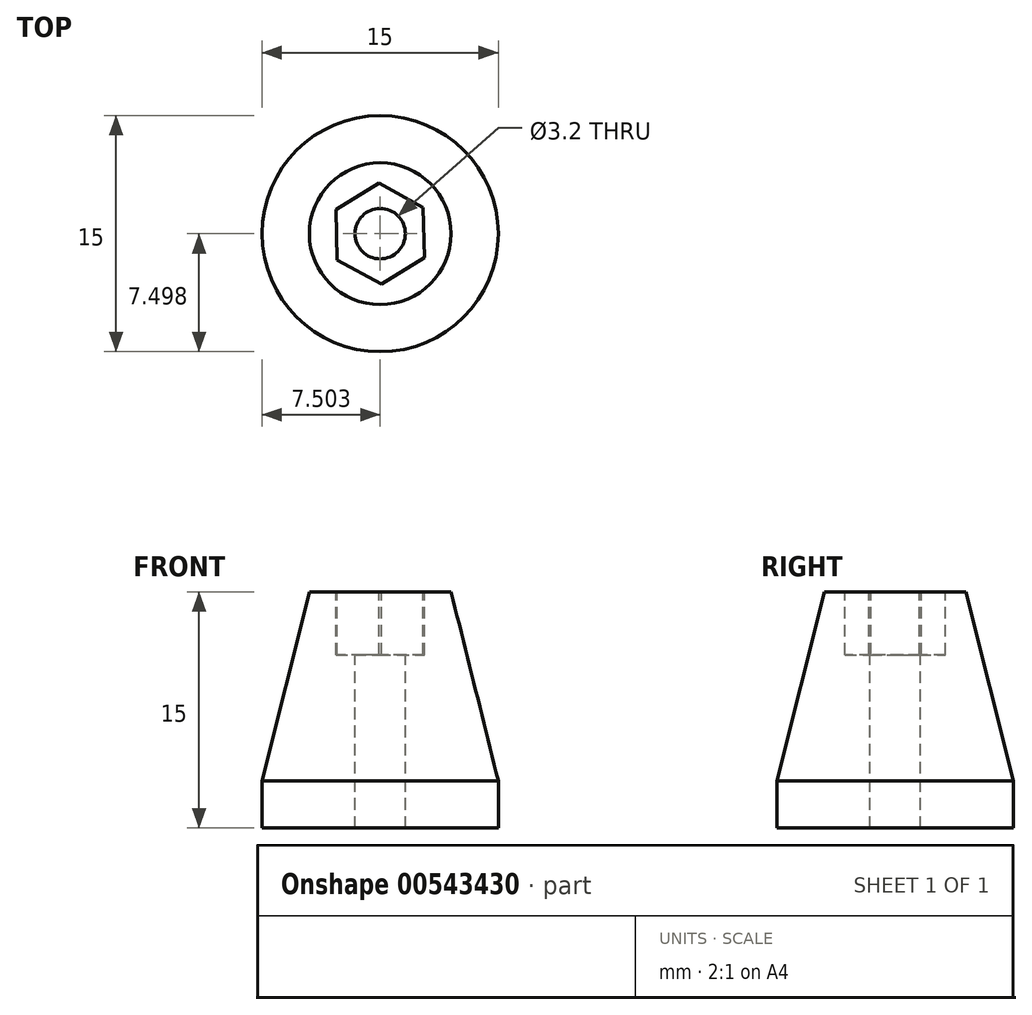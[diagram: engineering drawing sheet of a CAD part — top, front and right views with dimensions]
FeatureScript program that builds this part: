
annotation { "Feature Type Name" : "Feature", "Feature Type Description" : "" }
export const myFeature = defineFeature(function(context is Context, id is Id, definition is map)
    precondition{}
    {
        {
            var Q0;
            Q0=qCreatedBy(makeId("Top.planeOp"),FACE);
            var sketch = newSketch(context, id + "F0", { "sketchPlane" : qUnion([Q0])});
            skCircle(sketch, "E0", {"center": v(-11.83, 14.6) * mm, "radius": 7.5 * mm});
            skSolve(sketch);
        }
        {
            var Q0;
            Q0=makeQuery(id+"F0.imprint","IMPRINT",FACE,{"disambiguationData":[TD([[makeQuery(id+"F0.imprint","IMPRINT",EDGE,{"derivedFrom":sQuery(id+"F0.wireOp",EDGE,"E0")}),1.0]])]});
            extrude(context, id + "F1", {"entities" : qUnion([Q0]), "depth" : 3 * mm, "offsetDistance" : 25 * mm});
        }
        {
            var Q0;
            Q0=makeQuery(id+"F1.opExtrude","CAP_FACE",FACE,{"disambiguationData":[OSD([sQuery(id+"F0.wireOp",EDGE,"E0")])],"isStart":false});
            var sketch = newSketch(context, id + "F2", { "sketchPlane" : qUnion([Q0])});
            skCircle(sketch, "E1", {"center": v(-11.83, 14.6) * mm, "radius": 7.5 * mm});
            skSolve(sketch);
        }
        {
            var Q0;
            Q0 = qSketchRegion(id + "F2", true);
            var Q1;
            Q1=makeQuery(id+"F2.imprint","IMPRINT",FACE,{"disambiguationData":[TD([[makeQuery(id+"F2.imprint","IMPRINT",EDGE,{"derivedFrom":sQuery(id+"F2.wireOp",EDGE,"E1")}),1.0]])]});
            extrude(context, id + "F3", {"entities" : qUnion([Q0, Q1]), "operationType" : NewBodyOperationType.ADD, "depth" : 12 * mm, "offsetDistance" : 25 * mm});
        }
        {
            var Q0;
            Q0=makeQuery(id+"F3.opExtrude","CAP_FACE",FACE,{"disambiguationData":[OSD([sQuery(id+"F2.wireOp",EDGE,"E1")])],"isStart":false});
            chamfer(context, id + "F4", {"entities" : qUnion([Q0]), "chamferType" : ChamferType.TWO_OFFSETS, "width1" : 3 * mm, "oppositeDirection" : false, "width2" : 12 * mm});
        }
        {
            var Q0;
            Q0=makeQuery(id+"F3.opExtrude","CAP_FACE",FACE,{"disambiguationData":[OSD([sQuery(id+"F2.wireOp",EDGE,"E1")])],"isStart":false});
            var sketch = newSketch(context, id + "F5", { "sketchPlane" : qUnion([Q0])});
            skCircle(sketch, "E2.cCircle", {"center": v(-11.83, 14.6) * mm, "radius": 2.77 * mm, "construction": true});
            skLineSegment(sketch, "E2.0", {"start": v(-14.64, 16.13) * mm, "end": v(-11.9, 17.8) * mm});
            skLineSegment(sketch, "E2.1", {"start": v(-11.9, 17.8) * mm, "end": v(-9.1, 16.27) * mm});
            skLineSegment(sketch, "E2.2", {"start": v(-9.1, 16.27) * mm, "end": v(-9.01, 13.07) * mm});
            skLineSegment(sketch, "E2.3", {"start": v(-9.01, 13.07) * mm, "end": v(-11.74, 11.4) * mm});
            skLineSegment(sketch, "E2.4", {"start": v(-11.74, 11.4) * mm, "end": v(-14.56, 12.93) * mm});
            skLineSegment(sketch, "E2.5", {"start": v(-14.56, 12.93) * mm, "end": v(-14.64, 16.13) * mm});
            skPoint(sketch, "E2.0.midPoint", {"position": v(-13.27, 16.96) * mm});
            skSolve(sketch);
        }
        {
            var Q0;
            Q0 = qSketchRegion(id + "F5", true);
            extrude(context, id + "F6", {"entities" : qUnion([Q0]), "operationType" : NewBodyOperationType.REMOVE, "oppositeDirection" : true, "depth" : 4 * mm, "offsetDistance" : 25 * mm});
        }
        {
            var Q0;
            Q0=makeQuery(id+"F6.boolean.opBoolean","COPY",FACE,{"derivedFrom":makeQuery(id+"F6.opExtrude","CAP_FACE",FACE,{"disambiguationData":[OSD([sQuery(id+"F5.wireOp",EDGE,"E2.0"),sQuery(id+"F5.wireOp",EDGE,"E2.1"),sQuery(id+"F5.wireOp",EDGE,"E2.2"),sQuery(id+"F5.wireOp",EDGE,"E2.3"),sQuery(id+"F5.wireOp",EDGE,"E2.4"),sQuery(id+"F5.wireOp",EDGE,"E2.5")])],"isStart":false})});
            var sketch = newSketch(context, id + "F7", { "sketchPlane" : qUnion([Q0])});
            skCircle(sketch, "E3", {"center": v(-11.83, 14.6) * mm, "radius": 1.6 * mm});
            skSolve(sketch);
        }
        {
            var Q0;
            Q0 = qSketchRegion(id + "F7", true);
            extrude(context, id + "F8", {"entities" : qUnion([Q0]), "operationType" : NewBodyOperationType.REMOVE, "oppositeDirection" : true, "depth" : 11 * mm, "offsetDistance" : 25 * mm});
        }
    });
